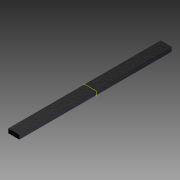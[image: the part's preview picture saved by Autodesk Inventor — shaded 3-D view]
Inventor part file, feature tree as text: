
AUTODESK INVENTOR PART (.ipt)
format: ipt  version: 2015 (Build 190159000, 159)  size: 71,680 bytes
history: native  units: mm
features: extrude x1
ambient origin geometry x8: Origin, YZ Plane, XZ Plane, XY Plane, X Axis, Y Axis, Z Axis, Center Point
bodies: Solid1 (feature_tree)
feature tree (1):
  extrude  "Extrusión1"  Depth=9.5mm
